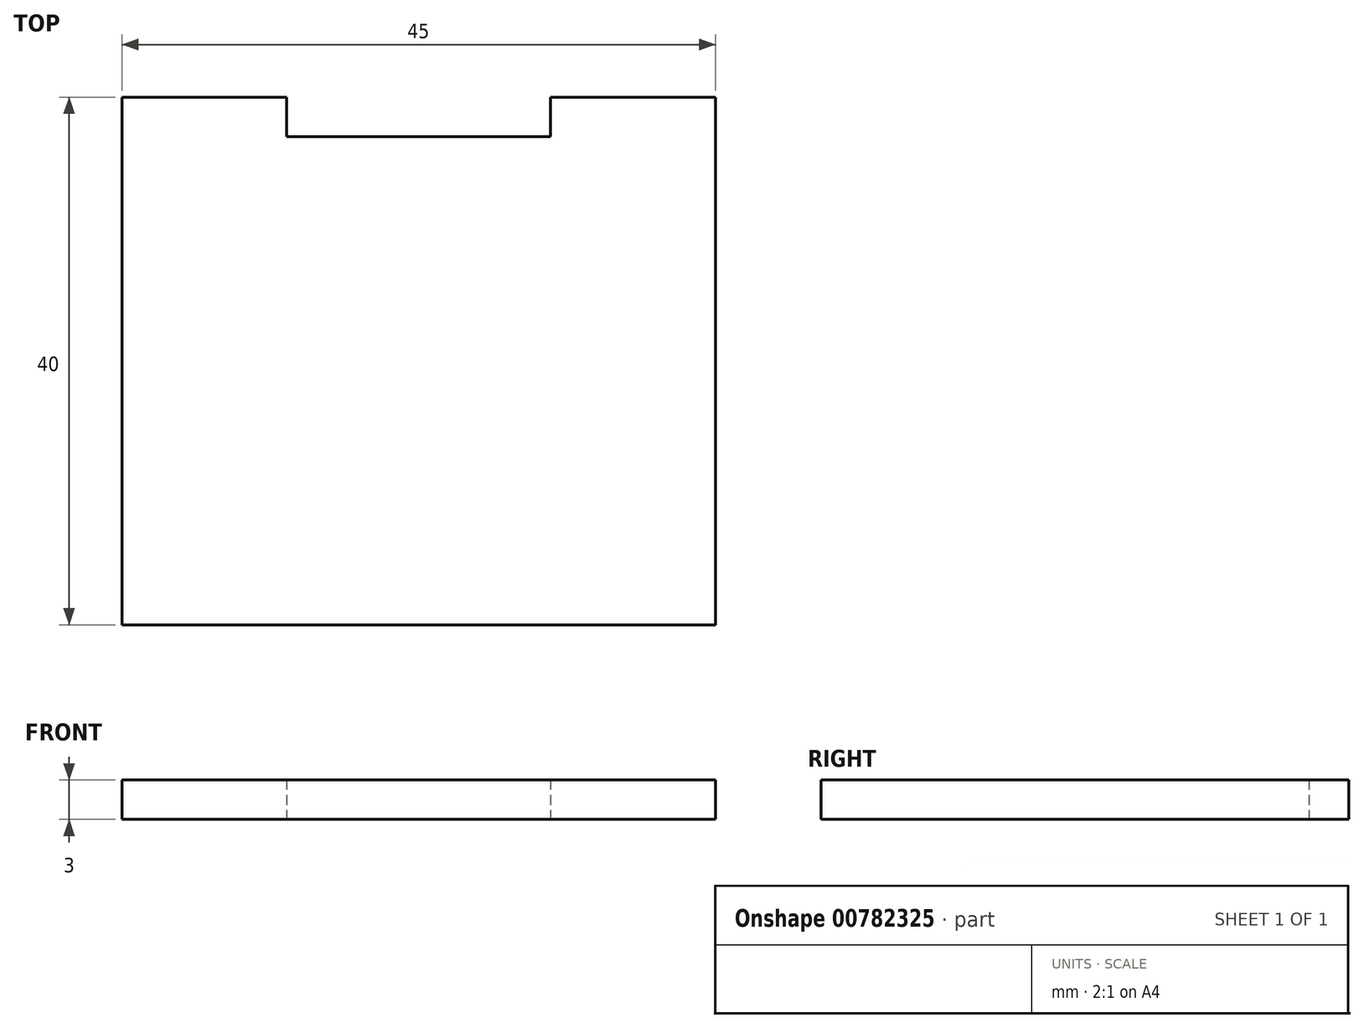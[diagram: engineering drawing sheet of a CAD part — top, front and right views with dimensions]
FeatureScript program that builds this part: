
annotation { "Feature Type Name" : "Feature", "Feature Type Description" : "" }
export const myFeature = defineFeature(function(context is Context, id is Id, definition is map)
    precondition{}
    {
        {
            var Q0;
            Q0=qCreatedBy(makeId("Top.planeOp"),FACE);
            var sketch = newSketch(context, id + "F0", { "sketchPlane" : qUnion([Q0])});
            skLineSegment(sketch, "E0.bottom", {"start": v(22.5, 20) * mm, "end": v(-22.5, 20) * mm});
            skLineSegment(sketch, "E0.top", {"start": v(22.5, -20) * mm, "end": v(-22.5, -20) * mm});
            skLineSegment(sketch, "E0.left", {"start": v(22.5, 20) * mm, "end": v(22.5, -20) * mm});
            skLineSegment(sketch, "E0.right", {"start": v(-22.5, 20) * mm, "end": v(-22.5, -20) * mm});
            skPoint(sketch, "E0.middle", {"position": v(0, 0) * mm});
            skLineSegment(sketch, "E1", {"start": v(-10, 17) * mm, "end": v(-10, 20) * mm});
            skLineSegment(sketch, "E2", {"start": v(-10, 17) * mm, "end": v(10, 17) * mm});
            skLineSegment(sketch, "E3", {"start": v(10, 20) * mm, "end": v(10, 17) * mm});
            skSolve(sketch);
        }
        {
            var Q0;
            Q0=makeQuery(id+"F0.imprint","IMPRINT",FACE,{"disambiguationData":[TD([[makeQuery(id+"F0.imprint","IMPRINT",EDGE,{"derivedFrom":sQuery(id+"F0.wireOp",EDGE,"E0.top")}),-1.0]])]});
            extrude(context, id + "F1", {"entities" : qUnion([Q0]), "depth" : 3 * mm, "offsetDistance" : 25 * mm});
        }
    });
